# Revit family: Columns_&_Screens-Teknion-RCFBF_Central_Screen_for_Spine_Desk_Fabric-R2019
name_source: partatom
category: Furniture
units: mm (PartAtom-declared; Revit-internal decimal feet)

## family parameters
Always vertical = Yes
Cut with Voids When Loaded = No
OmniClass Number = 23.40.20.00
OmniClass Title = General Furniture and Specialties
Room Calculation Point = No
Shared = Yes
Work Plane-Based = No

## types (5) — shared parameters
Assembly Code = E2020200
Manufacturer = Teknion
Manufacturer Fax = 416.661.4586
Part Number = RCFBF
Product Documentation Link = https://www.teknion.com
Product Line = Expansion Desking
Product Page URL = https://www.teknion.com
Series = Expansion Desking
Sustainability Data = https://www.teknion.com
URL = www.teknion.com
Unit Weight URL = http://www.teknion.com
Warranty = http://www.teknion.com

## per-type parameters (varying)
| type | Bottom of Screen | Description | Height | Model |
| Desk-Mounted, 51" High Datum Line With Desk-Mounted Option | 29 " | Central Screen for Spine Desk - Fabric, Desk-Mounted, 51" High Datum Line with Desk-Mounted option | 50.831 " | RCFBFD22__ |
| Worksurface-Mounted, 51" High Datum Line With Desk-Mounted Option | 29 " | Central Screen for Spine Desk - Fabric, Worksurface-Mounted, 51" High Datum Line with Desk-Mounted option | 50.831 " | RCFBFW22__ |
| Desk-Mounted, 42" High Datum Line With Desk-Mounted Option | 29 " | Central Screen for Spine Desk - Fabric, Desk-Mounted, 42" High Datum Line with Desk-Mounted option | 42 " | RCFBFD13__ |
| Worksurface-Mounted, 42" High Datum Line With Desk-Mounted Option | 29 " | Central Screen for Spine Desk - Fabric, Worksurface-Mounted, 42" High Datum Line with Desk-Mounted option | 42 " | RCFBFW13__ |
| Shelf-Mounted, 51" High Datum Line With Shelf-Mounted Option | 36.287 " | Central Screen for Spine Desk - Fabric, Shelf-Mounted, 51" High Datum Line with Shelf-Mounted option | 50.831 " | RCFBFS15__ |

## geometry (parser evidence)
native form markers: Sweep x3
no freeform markers — native parametric forms only
